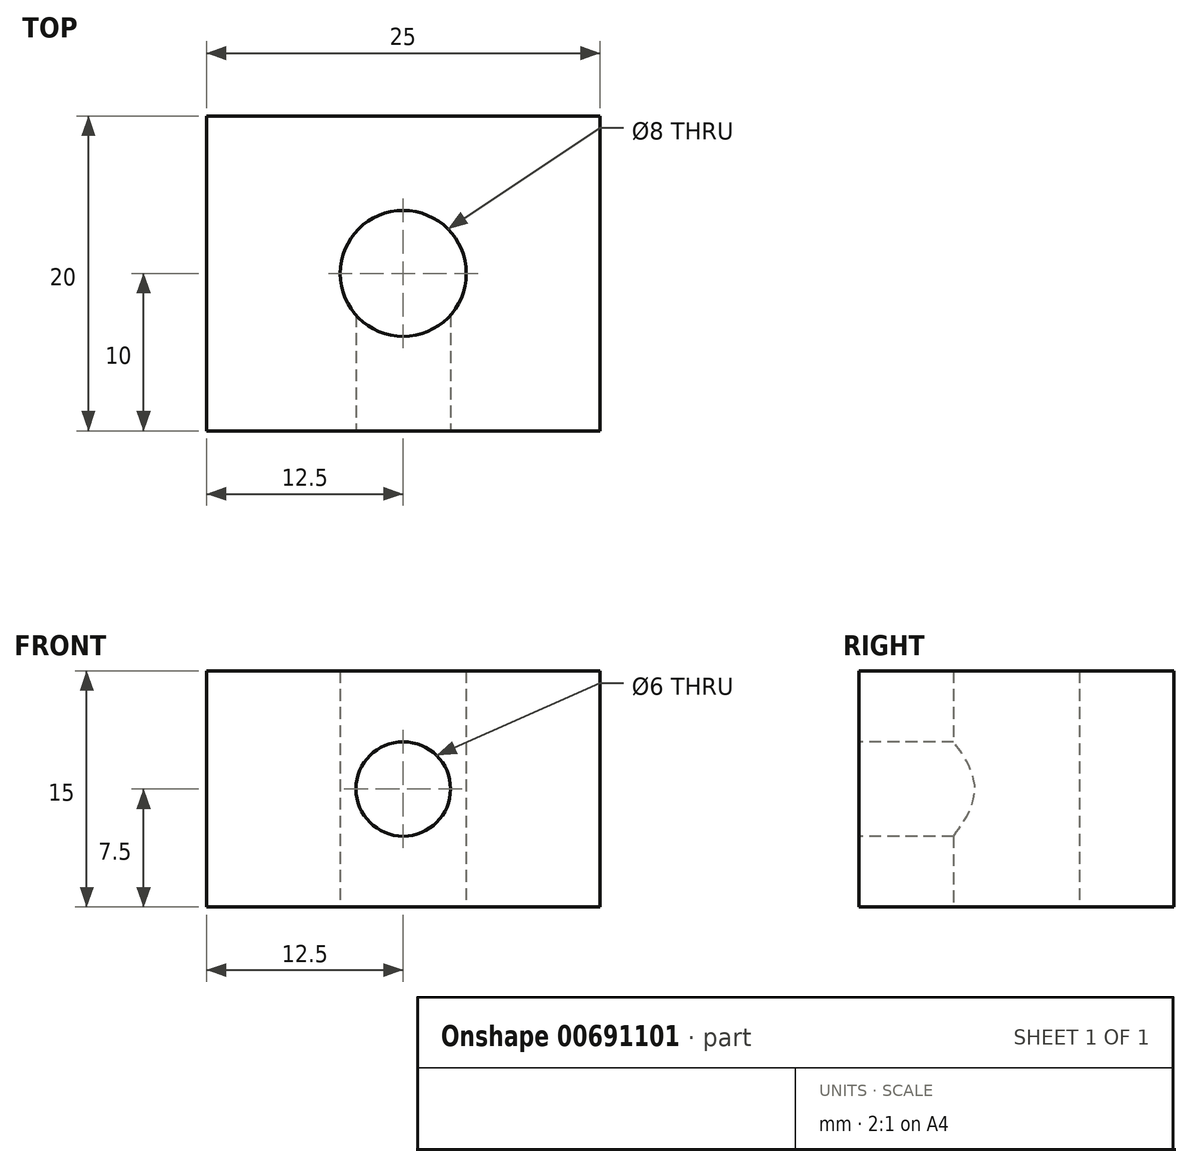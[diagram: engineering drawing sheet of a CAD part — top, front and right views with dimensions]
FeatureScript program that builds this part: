
annotation { "Feature Type Name" : "Feature", "Feature Type Description" : "" }
export const myFeature = defineFeature(function(context is Context, id is Id, definition is map)
    precondition{}
    {
        {
            var Q0;
            Q0=qCreatedBy(makeId("Top.planeOp"),FACE);
            var sketch = newSketch(context, id + "F0", { "sketchPlane" : qUnion([Q0])});
            skLineSegment(sketch, "E0.bottom", {"start": v(0, 0) * mm, "end": v(25, 0) * mm});
            skLineSegment(sketch, "E0.top", {"start": v(0, -20) * mm, "end": v(25, -20) * mm});
            skLineSegment(sketch, "E0.left", {"start": v(0, 0) * mm, "end": v(0, -20) * mm});
            skLineSegment(sketch, "E0.right", {"start": v(25, 0) * mm, "end": v(25, -20) * mm});
            skLineSegment(sketch, "E1", {"start": v(25, -10) * mm, "end": v(0, -10) * mm, "construction": true});
            skCircle(sketch, "E2", {"center": v(12.5, -10) * mm, "radius": 4 * mm});
            skSolve(sketch);
        }
        {
            var Q0;
            Q0=makeQuery(id+"F0.imprint","IMPRINT",FACE,{"disambiguationData":[TD([[makeQuery(id+"F0.imprint","IMPRINT",EDGE,{"derivedFrom":sQuery(id+"F0.wireOp",EDGE,"E0.bottom")}),-1.0]])]});
            extrude(context, id + "F1", {"entities" : qUnion([Q0]), "depth" : 15 * mm, "offsetDistance" : 25 * mm});
        }
        {
            var Q0;
            Q0=makeQuery(id+"F1.opExtrude","SWEPT_FACE",FACE,{"disambiguationData":[OSD([sQuery(id+"F0.wireOp",EDGE,"E0.top")])]});
            var sketch = newSketch(context, id + "F2", { "sketchPlane" : qUnion([Q0])});
            skLineSegment(sketch, "E3", {"start": v(0, 7.5) * mm, "end": v(25, 7.5) * mm, "construction": true});
            skCircle(sketch, "E4", {"center": v(12.5, 7.5) * mm, "radius": 3 * mm});
            skSolve(sketch);
        }
        {
            var Q0;
            Q0=makeQuery(id+"F2.imprint","IMPRINT",FACE,{"disambiguationData":[TD([[makeQuery(id+"F2.imprint","IMPRINT",EDGE,{"derivedFrom":sQuery(id+"F2.wireOp",EDGE,"E4")}),1.0]])]});
            extrude(context, id + "F3", {"entities" : qUnion([Q0]), "operationType" : NewBodyOperationType.REMOVE, "oppositeDirection" : true, "depth" : 10 * mm, "offsetDistance" : 25 * mm});
        }
    });
